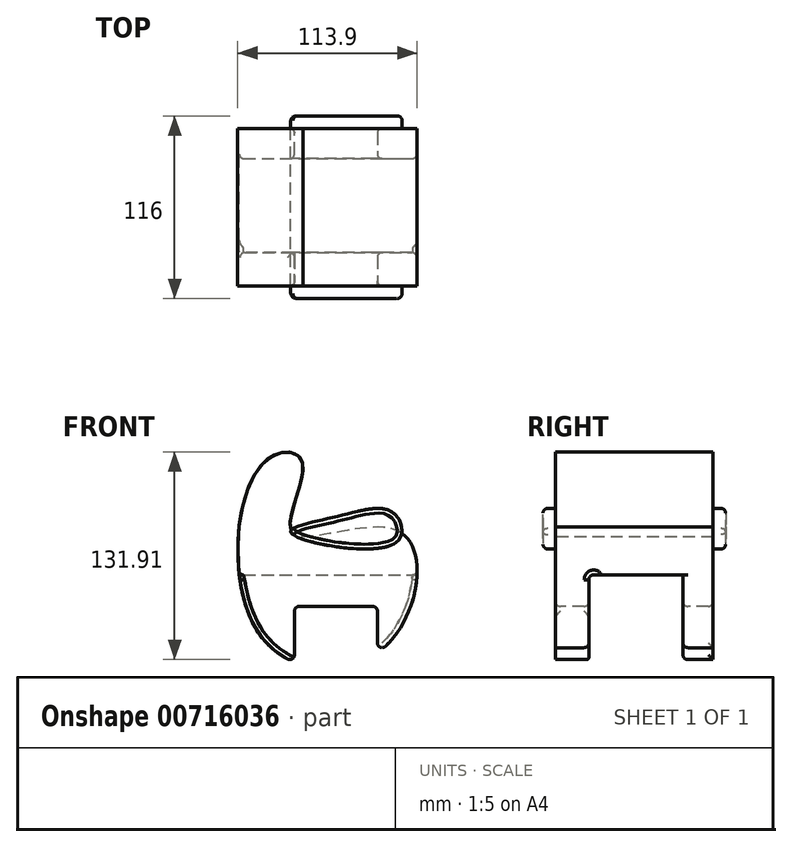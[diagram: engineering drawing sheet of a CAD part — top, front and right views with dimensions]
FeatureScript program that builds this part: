
annotation { "Feature Type Name" : "Feature", "Feature Type Description" : "" }
export const myFeature = defineFeature(function(context is Context, id is Id, definition is map)
    precondition{}
    {
        {
            var Q0;
            Q0=qCreatedBy(makeId("Front.planeOp"),FACE);
            var sketch = newSketch(context, id + "F0", { "sketchPlane" : qUnion([Q0])});
            skFitSpline(sketch, "E0", {"points": [v(-43.33, 47.77) * mm, v(-44.81, -63.45) * mm, v(34.46, -68.48) * mm, v(42.45, 3.7) * mm, v(-25.3, 2.81) * mm, v(-19.08, 47.77) * mm, v(-43.33, 47.77) * mm]});
            skSolve(sketch);
        }
        {
            var Q0;
            Q0=makeQuery(id+"F0.imprint","IMPRINT",FACE,{"disambiguationData":[TD([[makeQuery(id+"F0.imprint","IMPRINT",EDGE,{"derivedFrom":sQuery(id+"F0.wireOp",EDGE,"E0")}),1.0]])]});
            extrude(context, id + "F1", {"entities" : qUnion([Q0]), "depth" : 100 * mm, "offsetDistance" : 25.4 * mm});
        }
        {
            var Q0;
            Q0=qCreatedBy(makeId("Front.planeOp"),FACE);
            var sketch = newSketch(context, id + "F2", { "sketchPlane" : qUnion([Q0])});
            skFitSpline(sketch, "E1", {"points": [v(-26.05, 2.75) * mm, v(2.28, 13.12) * mm, v(38.78, 15.52) * mm, v(39.98, -3.63) * mm, v(-26.05, 2.75) * mm]});
            skSolve(sketch);
        }
        {
            var Q0;
            Q0 = qSketchRegion(id + "F2", true);
            extrude(context, id + "F3", {"entities" : qUnion([Q0]), "operationType" : NewBodyOperationType.ADD, "oppositeDirection" : true, "depth" : 8 * mm, "offsetDistance" : 25 * mm});
        }
        {
            var Q0;
            Q0=qCreatedBy(makeId("Front.planeOp"),FACE);
            cPlane(context, id + "F4", {"entities" : qUnion([Q0]), "cplaneType" : CPlaneType.OFFSET, "offset" : 50 * mm, "width" : 150 * mm, "height" : 150 * mm});
        }
        {
            var Q0;
            Q0=makeQuery(id+"F1.opExtrude","SWEPT_BODY",BODY,{"disambiguationData":[OSD([sQuery(id+"F0.wireOp",EDGE,"E0")])]});
            var Q1;
            Q1=qCreatedBy(id+"F4.planeOp",FACE);
            mirror(context, id + "F5", {"operationType" : NewBodyOperationType.ADD, "entities" : qUnion([Q0]), "mirrorPlane" : qUnion([Q1])});
        }
        {
            var Q0;
            Q0=qCreatedBy(makeId("Front.planeOp"),FACE);
            var sketch = newSketch(context, id + "F6", { "sketchPlane" : qUnion([Q0])});
            skLineSegment(sketch, "E2.bottom", {"start": v(-24.04, -43.8) * mm, "end": v(28.63, -43.8) * mm});
            skLineSegment(sketch, "E2.top", {"start": v(-24.04, -83.9) * mm, "end": v(28.63, -83.9) * mm});
            skLineSegment(sketch, "E2.left", {"start": v(-24.04, -43.8) * mm, "end": v(-24.04, -83.9) * mm});
            skLineSegment(sketch, "E2.right", {"start": v(28.63, -43.8) * mm, "end": v(28.63, -83.9) * mm});
            skSolve(sketch);
        }
        {
            var Q0;
            Q0 = qSketchRegion(id + "F6", true);
            extrude(context, id + "F7", {"entities" : qUnion([Q0]), "operationType" : NewBodyOperationType.REMOVE, "oppositeDirection" : true, "depth" : 100 * mm, "offsetDistance" : 25 * mm, "hasSecondDirection" : true, "secondDirectionOppositeDirection" : false, "secondDirectionDepth" : 100 * mm});
        }
        {
            var Q0;
            Q0=qCreatedBy(makeId("Right.planeOp"),FACE);
            var sketch = newSketch(context, id + "F8", { "sketchPlane" : qUnion([Q0])});
            skLineSegment(sketch, "E3.bottom", {"start": v(-78.88, -23.75) * mm, "end": v(-19.11, -23.75) * mm});
            skLineSegment(sketch, "E3.top", {"start": v(-78.88, -79.64) * mm, "end": v(-19.11, -79.64) * mm});
            skLineSegment(sketch, "E3.left", {"start": v(-78.88, -23.75) * mm, "end": v(-78.88, -79.64) * mm});
            skLineSegment(sketch, "E3.right", {"start": v(-19.11, -23.75) * mm, "end": v(-19.11, -79.64) * mm});
            skSolve(sketch);
        }
        {
            var Q0;
            Q0 = qSketchRegion(id + "F8", true);
            extrude(context, id + "F9", {"entities" : qUnion([Q0]), "operationType" : NewBodyOperationType.REMOVE, "oppositeDirection" : true, "depth" : 100 * mm, "offsetDistance" : 25 * mm, "hasSecondDirection" : true, "secondDirectionOppositeDirection" : false, "secondDirectionDepth" : 100 * mm});
        }
        {
            var Q0;
            Q0=makeQuery(id+"F9.boolean.opBoolean","INTERSECT",EDGE,{"derivedFrom":[makeQuery(id+"F7.boolean.opBoolean","COPY",FACE,{"derivedFrom":makeQuery(id+"F7.opExtrude","SWEPT_FACE",FACE,{"disambiguationData":[OSD([sQuery(id+"F6.wireOp",EDGE,"E2.bottom")])]})}),makeQuery(id+"F9.opExtrude","SWEPT_FACE",FACE,{"disambiguationData":[OSD([sQuery(id+"F8.wireOp",EDGE,"E3.left")])]})]});
            var Q1;
            Q1=makeQuery(id+"F9.boolean.opBoolean","SPLIT",FACE,{"disambiguationData":[TD([makeQuery(id+"F1.opExtrude","CAP_FACE",FACE,{"disambiguationData":[OSD([sQuery(id+"F0.wireOp",EDGE,"E0")])],"isStart":false})])],"derivedFrom":makeQuery(id+"F7.boolean.opBoolean","COPY",FACE,{"derivedFrom":makeQuery(id+"F7.opExtrude","SWEPT_FACE",FACE,{"disambiguationData":[OSD([sQuery(id+"F6.wireOp",EDGE,"E2.bottom")])]})})});
            var Q2;
            {var subQ0=sQuery(id+"F0.wireOp",EDGE,"E0");var subQ1=makeQuery(id+"F1.opExtrude","SWEPT_FACE",FACE,{"disambiguationData":[OSD([subQ0])]});var subQ2=makeQuery(id+"F7.opExtrude","SWEPT_FACE",FACE,{"disambiguationData":[OSD([sQuery(id+"F6.wireOp",EDGE,"E2.left")])]});Q2=makeQuery(id+"F9.boolean.opBoolean","SPLIT",EDGE,{"disambiguationData":[TD([makeQuery(id+"F1.opExtrude","CAP_FACE",FACE,{"disambiguationData":[OSD([subQ0])],"isStart":false})])],"derivedFrom":makeQuery(id+"F7.boolean.opBoolean","INTERSECT",EDGE,{"derivedFrom":[subQ1,subQ2]})});}
            var Q3;
            {var subQ0=sQuery(id+"F0.wireOp",EDGE,"E0");var subQ1=makeQuery(id+"F1.opExtrude","SWEPT_FACE",FACE,{"disambiguationData":[OSD([subQ0])]});var subQ2=makeQuery(id+"F7.opExtrude","SWEPT_FACE",FACE,{"disambiguationData":[OSD([sQuery(id+"F6.wireOp",EDGE,"E2.right")])]});Q3=makeQuery(id+"F9.boolean.opBoolean","SPLIT",EDGE,{"disambiguationData":[TD([makeQuery(id+"F1.opExtrude","CAP_FACE",FACE,{"disambiguationData":[OSD([subQ0])],"isStart":false})])],"derivedFrom":makeQuery(id+"F7.boolean.opBoolean","INTERSECT",EDGE,{"derivedFrom":[subQ1,subQ2]})});}
            var Q4;
            Q4=makeQuery(id+"F9.boolean.opBoolean","INTERSECT",EDGE,{"derivedFrom":[makeQuery(id+"F7.boolean.opBoolean","COPY",FACE,{"derivedFrom":makeQuery(id+"F7.opExtrude","SWEPT_FACE",FACE,{"disambiguationData":[OSD([sQuery(id+"F6.wireOp",EDGE,"E2.right")])]})}),makeQuery(id+"F9.opExtrude","SWEPT_FACE",FACE,{"disambiguationData":[OSD([sQuery(id+"F8.wireOp",EDGE,"E3.left")])]})]});
            var Q5;
            Q5=makeQuery(id+"F7.boolean.opBoolean","INTERSECT",EDGE,{"derivedFrom":[makeQuery(id+"F1.opExtrude","CAP_FACE",FACE,{"disambiguationData":[OSD([sQuery(id+"F0.wireOp",EDGE,"E0")])],"isStart":true}),makeQuery(id+"F7.opExtrude","SWEPT_FACE",FACE,{"disambiguationData":[OSD([sQuery(id+"F6.wireOp",EDGE,"E2.bottom")])]})]});
            var Q6;
            Q6=makeQuery(id+"F9.boolean.opBoolean","SPLIT",FACE,{"disambiguationData":[TD([makeQuery(id+"F1.opExtrude","CAP_FACE",FACE,{"disambiguationData":[OSD([sQuery(id+"F0.wireOp",EDGE,"E0")])],"isStart":true})])],"derivedFrom":makeQuery(id+"F7.boolean.opBoolean","COPY",FACE,{"derivedFrom":makeQuery(id+"F7.opExtrude","SWEPT_FACE",FACE,{"disambiguationData":[OSD([sQuery(id+"F6.wireOp",EDGE,"E2.bottom")])]})})});
            var Q7;
            Q7=makeQuery(id+"F7.boolean.opBoolean","INTERSECT",EDGE,{"derivedFrom":[makeQuery(id+"F1.opExtrude","CAP_FACE",FACE,{"disambiguationData":[OSD([sQuery(id+"F0.wireOp",EDGE,"E0")])],"isStart":true}),makeQuery(id+"F7.opExtrude","SWEPT_FACE",FACE,{"disambiguationData":[OSD([sQuery(id+"F6.wireOp",EDGE,"E2.right")])]})]});
            var Q8;
            Q8=makeQuery(id+"F9.boolean.opBoolean","INTERSECT",EDGE,{"derivedFrom":[makeQuery(id+"F7.boolean.opBoolean","COPY",FACE,{"derivedFrom":makeQuery(id+"F7.opExtrude","SWEPT_FACE",FACE,{"disambiguationData":[OSD([sQuery(id+"F6.wireOp",EDGE,"E2.right")])]})}),makeQuery(id+"F9.opExtrude","SWEPT_FACE",FACE,{"disambiguationData":[OSD([sQuery(id+"F8.wireOp",EDGE,"E3.right")])]})]});
            var Q9;
            {var subQ0=sQuery(id+"F0.wireOp",EDGE,"E0");var subQ1=makeQuery(id+"F1.opExtrude","SWEPT_FACE",FACE,{"disambiguationData":[OSD([subQ0])]});var subQ2=makeQuery(id+"F7.opExtrude","SWEPT_FACE",FACE,{"disambiguationData":[OSD([sQuery(id+"F6.wireOp",EDGE,"E2.right")])]});Q9=makeQuery(id+"F9.boolean.opBoolean","SPLIT",EDGE,{"disambiguationData":[TD([makeQuery(id+"F1.opExtrude","CAP_FACE",FACE,{"disambiguationData":[OSD([subQ0])],"isStart":true})])],"derivedFrom":makeQuery(id+"F7.boolean.opBoolean","INTERSECT",EDGE,{"derivedFrom":[subQ1,subQ2]})});}
            var Q10;
            {var subQ0=sQuery(id+"F0.wireOp",EDGE,"E0");Q10=makeQuery(id+"F9.boolean.opBoolean","SPLIT",FACE,{"disambiguationData":[TD([makeQuery(id+"F1.opExtrude","CAP_FACE",FACE,{"disambiguationData":[OSD([subQ0])],"isStart":true})])],"derivedFrom":makeQuery(id+"F7.boolean.opBoolean","COPY",FACE,{"derivedFrom":makeQuery(id+"F7.opExtrude","SWEPT_FACE",FACE,{"disambiguationData":[OSD([sQuery(id+"F6.wireOp",EDGE,"E2.left")])]})})});}
            var Q11;
            {var subQ0=sQuery(id+"F0.wireOp",EDGE,"E0");var subQ1=makeQuery(id+"F1.opExtrude","SWEPT_FACE",FACE,{"disambiguationData":[OSD([subQ0])]});var subQ2=makeQuery(id+"F7.opExtrude","SWEPT_FACE",FACE,{"disambiguationData":[OSD([sQuery(id+"F6.wireOp",EDGE,"E2.left")])]});Q11=makeQuery(id+"F9.boolean.opBoolean","SPLIT",EDGE,{"disambiguationData":[TD([makeQuery(id+"F1.opExtrude","CAP_FACE",FACE,{"disambiguationData":[OSD([subQ0])],"isStart":true})])],"derivedFrom":makeQuery(id+"F7.boolean.opBoolean","INTERSECT",EDGE,{"derivedFrom":[subQ1,subQ2]})});}
            var Q12;
            Q12=makeQuery(id+"F9.boolean.opBoolean","INTERSECT",EDGE,{"disambiguationData":[OD(0.0)],"derivedFrom":[makeQuery(id+"F1.opExtrude","SWEPT_FACE",FACE,{"disambiguationData":[OSD([sQuery(id+"F0.wireOp",EDGE,"E0")])]}),makeQuery(id+"F9.opExtrude","SWEPT_FACE",FACE,{"disambiguationData":[OSD([sQuery(id+"F8.wireOp",EDGE,"E3.left")])]})]});
            var Q13;
            Q13=makeQuery(id+"F9.boolean.opBoolean","INTERSECT",EDGE,{"disambiguationData":[OD(1.0)],"derivedFrom":[makeQuery(id+"F1.opExtrude","SWEPT_FACE",FACE,{"disambiguationData":[OSD([sQuery(id+"F0.wireOp",EDGE,"E0")])]}),makeQuery(id+"F9.opExtrude","SWEPT_FACE",FACE,{"disambiguationData":[OSD([sQuery(id+"F8.wireOp",EDGE,"E3.left")])]})]});
            var Q14;
            Q14=makeQuery(id+"F9.boolean.opBoolean","COPY",EDGE,{"derivedFrom":makeQuery(id+"F9.opExtrude","SWEPT_EDGE",EDGE,{"disambiguationData":[OSD([sQuery(id+"F8.wireOp",EDGE,"E3.bottom"),sQuery(id+"F8.wireOp",EDGE,"E3.left")])]})});
            var Q15;
            Q15=makeQuery(id+"F9.boolean.opBoolean","INTERSECT",EDGE,{"disambiguationData":[OD(1.0)],"derivedFrom":[makeQuery(id+"F1.opExtrude","SWEPT_FACE",FACE,{"disambiguationData":[OSD([sQuery(id+"F0.wireOp",EDGE,"E0")])]}),makeQuery(id+"F9.opExtrude","SWEPT_FACE",FACE,{"disambiguationData":[OSD([sQuery(id+"F8.wireOp",EDGE,"E3.right")])]})]});
            var Q16;
            Q16=makeQuery(id+"F9.boolean.opBoolean","INTERSECT",EDGE,{"disambiguationData":[OD(0.0)],"derivedFrom":[makeQuery(id+"F1.opExtrude","SWEPT_FACE",FACE,{"disambiguationData":[OSD([sQuery(id+"F0.wireOp",EDGE,"E0")])]}),makeQuery(id+"F9.opExtrude","SWEPT_FACE",FACE,{"disambiguationData":[OSD([sQuery(id+"F8.wireOp",EDGE,"E3.right")])]})]});
            var Q17;
            Q17=makeQuery(id+"F3.opExtrude","CAP_FACE",FACE,{"disambiguationData":[OSD([sQuery(id+"F2.wireOp",EDGE,"E1")])],"isStart":false});
            var Q18;
            Q18=makeQuery(id+"F5.opPattern","COPY",FACE,{"derivedFrom":makeQuery(id+"F3.opExtrude","CAP_FACE",FACE,{"disambiguationData":[OSD([sQuery(id+"F2.wireOp",EDGE,"E1")])],"isStart":false}),"instanceName":"1"});
            fillet(context, id + "F10", {"entities" : qUnion([Q0, Q1, Q2, Q3, Q4, Q5, Q6, Q7, Q8, Q9, Q10, Q11, Q12, Q13, Q14, Q15, Q16, Q17, Q18]), "radius" : 3 * mm, "tangentPropagation" : true, "allowEdgeOverflow" : false});
        }
    });
